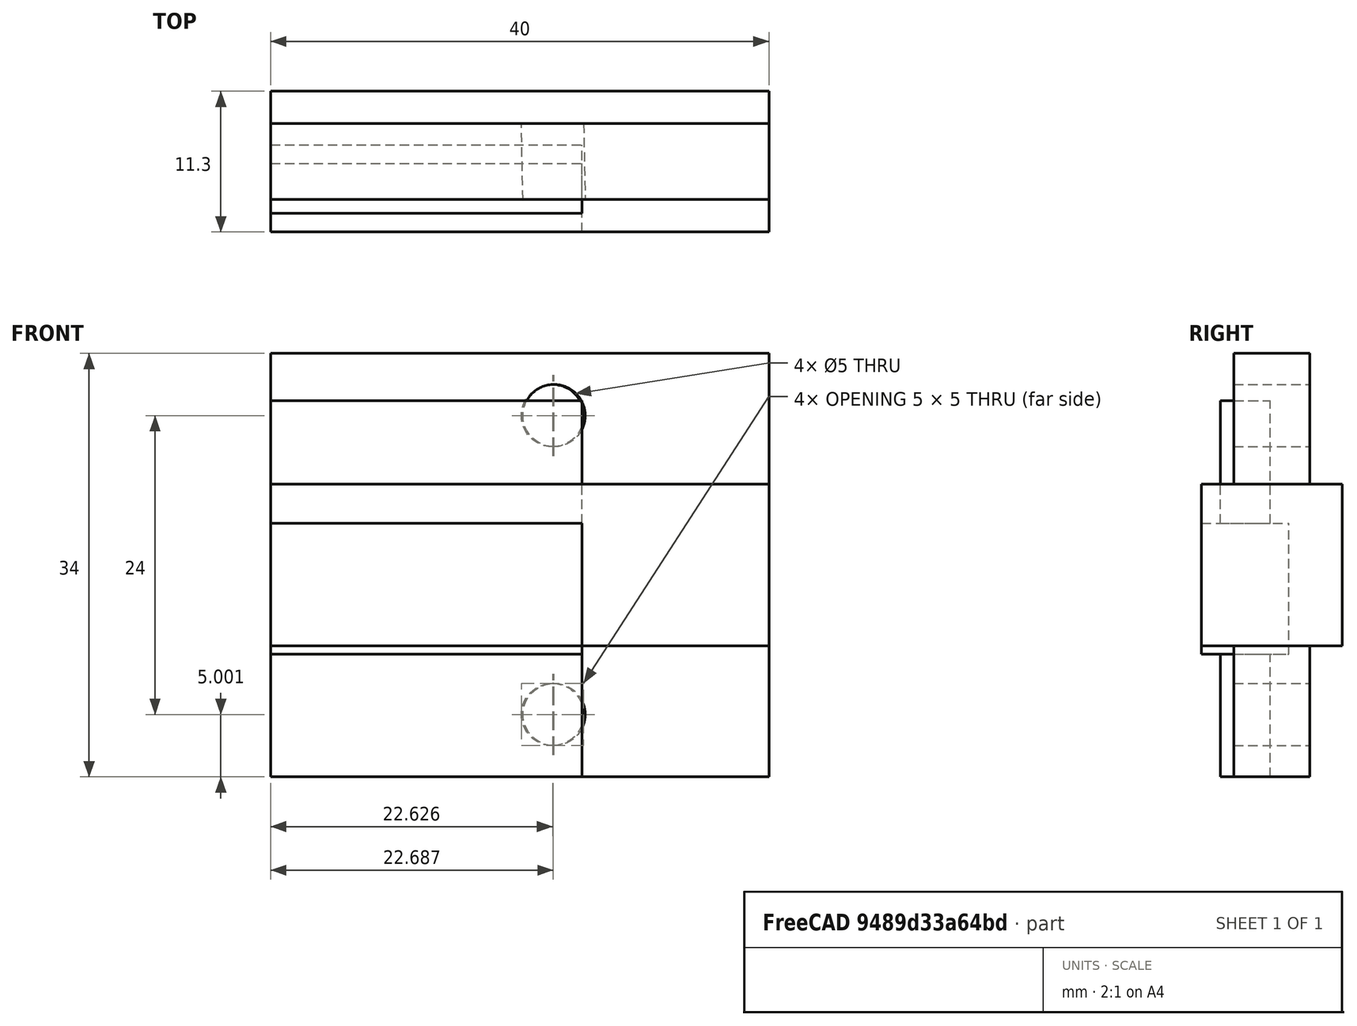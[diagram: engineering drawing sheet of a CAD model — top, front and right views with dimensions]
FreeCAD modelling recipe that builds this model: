
FCSTD DOCUMENT  (FreeCAD 0.20R29410 (Git))
Label: crimper_adapter
License: All rights reserved
LicenseURL: http://en.wikipedia.org/wiki/All_rights_reserved
objects: Part::Box×9, Part::Cylinder×4, Part::Cut×4, Part::MultiFuse×1
note: 18 computed .brp shape members not serialized (recipe doc carries the construction recipe); baked Part::Feature solids carry a one-line shape summary decoded from their .brp

FEATURE [Part::Box] Box  label="Cube"
  AttacherType = Attacher::AttachEngine3D
  Height = 13
  Length = 40
  Placement = pos=(0,0,10.5) rot=(0,0,1;0rad)
  Width = 11.3
FEATURE [Part::Box] Box001  label="Cube001"
  AttacherType = Attacher::AttachEngine3D
  Height = 10.5
  Length = 40
  Placement = pos=(0,2.6,23.5) rot=(0,0,1;0rad)
  Width = 6.1
FEATURE [Part::Cylinder] Cylinder
  Angle = 360
  AttacherType = Attacher::AttachEngine3D
  FirstAngle = 0
  Height = 20
  Placement = pos=(22.5,15,29) rot=(0.9999,0.009999,0.009999;1.5708rad)
  Radius = 2.5
  SecondAngle = 0
FEATURE [Part::Box] Box002  label="Cube002"
  AttacherType = Attacher::AttachEngine3D
  Height = 10.5
  Length = 40
  Placement = pos=(0,2.6,0) rot=(0,0,1;0rad)
  Width = 6.1
FEATURE [Part::Cylinder] Cylinder001
  Angle = 360
  AttacherType = Attacher::AttachEngine3D
  FirstAngle = 0
  Height = 20
  Placement = pos=(22.5,15,5) rot=(0.9999,0.009999,0.009999;1.5708rad)
  Radius = 2.5
  SecondAngle = 0
FEATURE [Part::Cut] Cut
  Base = -> Box001
  Tool = -> Cylinder
FEATURE [Part::Cut] Cut001
  Base = -> Box002
  Tool = -> Cylinder001
FEATURE [Part::MultiFuse] Fusion
  Shapes = -> [Cut,Box,Cut001]
FEATURE [Part::Box] Box003  label="Cube003"
  AttacherType = Attacher::AttachEngine3D
  Height = 13
  Length = 40
  Placement = pos=(0,0,10.5) rot=(0,0,1;0rad)
  Width = 11.3
FEATURE [Part::Box] Box004  label="Cube004"
  AttacherType = Attacher::AttachEngine3D
  Height = 10.5
  Length = 40
  Placement = pos=(0,2.6,23.5) rot=(0,0,1;0rad)
  Width = 6.1
FEATURE [Part::Box] Box005  label="Cube005"
  AttacherType = Attacher::AttachEngine3D
  Height = 10.5
  Length = 40
  Placement = pos=(0,2.6,0) rot=(0,0,1;0rad)
  Width = 6.1
FEATURE [Part::Cylinder] Cylinder002
  Angle = 360
  AttacherType = Attacher::AttachEngine3D
  FirstAngle = 0
  Height = 20
  Placement = pos=(22.5,15,29) rot=(0.9999,0.009999,0.009999;1.5708rad)
  Radius = 2.5
  SecondAngle = 0
FEATURE [Part::Cut] Cut002
  Base = -> Box004
  Tool = -> Cylinder002
FEATURE [Part::Cylinder] Cylinder003
  Angle = 360
  AttacherType = Attacher::AttachEngine3D
  FirstAngle = 0
  Height = 20
  Placement = pos=(22.5,15,5) rot=(0.9999,0.009999,0.009999;1.5708rad)
  Radius = 2.5
  SecondAngle = 0
FEATURE [Part::Cut] Cut003
  Base = -> Box005
  Tool = -> Cylinder003
FEATURE [Part::Box] Box006  label="Cube006"
  AttacherType = Attacher::AttachEngine3D
  Height = 10.5
  Length = 25
  Placement = pos=(0,0,9.85) rot=(0,0,1;0rad)
  Width = 7
FEATURE [Part::Box] Box007  label="Cube007"
  AttacherType = Attacher::AttachEngine3D
  Height = 9.85
  Length = 25
  Placement = pos=(0,1.5,20.35) rot=(0,0,1;0rad)
  Width = 4
FEATURE [Part::Box] Box008  label="Cube008"
  AttacherType = Attacher::AttachEngine3D
  Height = 9.85
  Length = 25
  Placement = pos=(0,1.5,0) rot=(0,0,1;0rad)
  Width = 4
